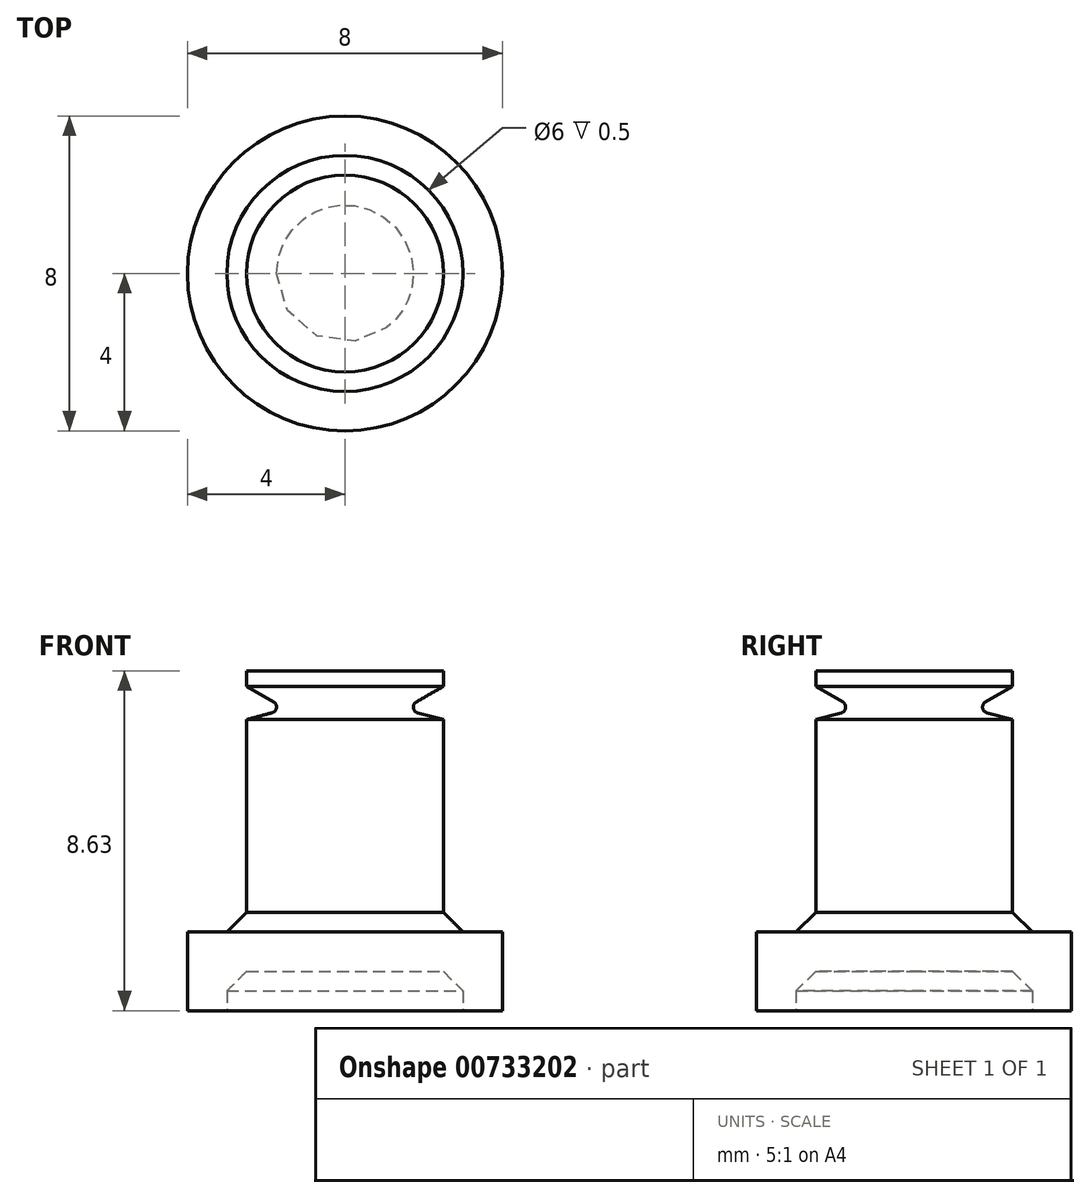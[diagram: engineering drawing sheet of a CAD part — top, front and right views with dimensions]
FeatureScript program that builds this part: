
annotation { "Feature Type Name" : "Feature", "Feature Type Description" : "" }
export const myFeature = defineFeature(function(context is Context, id is Id, definition is map)
    precondition{}
    {
        {
            var Q0;
            Q0=qCreatedBy(makeId("Right.planeOp"),FACE);
            var sketch = newSketch(context, id + "F0", { "sketchPlane" : qUnion([Q0])});
            skLineSegment(sketch, "E0", {"start": v(0, 0) * mm, "end": v(0, 36.44) * mm, "construction": true});
            skLineSegment(sketch, "E1", {"start": v(0, 0) * mm, "end": v(4, 0) * mm});
            skLineSegment(sketch, "E2", {"start": v(4, 0) * mm, "end": v(4, 2) * mm});
            skLineSegment(sketch, "E3", {"start": v(4, 2) * mm, "end": v(2.5, 2) * mm});
            skLineSegment(sketch, "E4", {"start": v(2.5, 2) * mm, "end": v(2.5, 8.63) * mm});
            skLineSegment(sketch, "E5", {"start": v(2.5, 8.63) * mm, "end": v(0, 8.63) * mm});
            skLineSegment(sketch, "E6", {"start": v(2.5, 8.24) * mm, "end": v(1.5, 7.66) * mm});
            skLineSegment(sketch, "E7", {"start": v(1.5, 7.66) * mm, "end": v(2.5, 7.4) * mm});
            skLineSegment(sketch, "E8", {"start": v(0, 8.63) * mm, "end": v(0, 0) * mm});
            skLineSegment(sketch, "E9.bottom", {"start": v(0, 0) * mm, "end": v(3, 0) * mm});
            skLineSegment(sketch, "E9.top", {"start": v(0, 1) * mm, "end": v(3, 1) * mm});
            skLineSegment(sketch, "E9.left", {"start": v(0, 0) * mm, "end": v(0, 1) * mm});
            skLineSegment(sketch, "E9.right", {"start": v(3, 0) * mm, "end": v(3, 1) * mm});
            skSolve(sketch);
        }
        {
            var Q0;
            {var subQ6=sQuery(id+"F0.wireOp",EDGE,"E2");Q0=makeQuery(id+"F0.imprint","IMPRINT",FACE,{"disambiguationData":[TD([[makeQuery(id+"F0.imprint","IMPRINT",EDGE,{"derivedFrom":subQ6}),1.0]])]});}
            var Q1;
            Q1=sQuery(id+"F0.wireOp",EDGE,"E0");
            revolve(context, id + "F1", {"surfaceOperationType" : NewSurfaceOperationType.NEW, "entities" : qUnion([Q0]), "axis" : qUnion([Q1]), "revolveType" : RevolveType.FULL});
        }
        {
            var Q0;
            Q0=makeQuery(id+"F1.opRevolve","SWEPT_EDGE",EDGE,{"disambiguationData":[OSD([sQuery(id+"F0.wireOp",EDGE,"E3"),sQuery(id+"F0.wireOp",EDGE,"E4")])]});
            var Q1;
            Q1=makeQuery(id+"F1.opRevolve","SWEPT_EDGE",EDGE,{"disambiguationData":[OSD([sQuery(id+"F0.wireOp",EDGE,"E9.top"),sQuery(id+"F0.wireOp",EDGE,"E9.right")])]});
            chamfer(context, id + "F2", {"entities" : qUnion([Q0, Q1]), "width" : 0.5 * mm, "tangentPropagation" : true});
        }
        {
            var Q0;
            Q0=makeQuery(id+"F1.opRevolve","SWEPT_EDGE",EDGE,{"disambiguationData":[OSD([sQuery(id+"F0.wireOp",EDGE,"E6"),sQuery(id+"F0.wireOp",EDGE,"E7")])]});
            fillet(context, id + "F3", {"entities" : qUnion([Q0]), "radius" : 0.15 * mm, "tangentPropagation" : true, "allowEdgeOverflow" : false});
        }
    });
